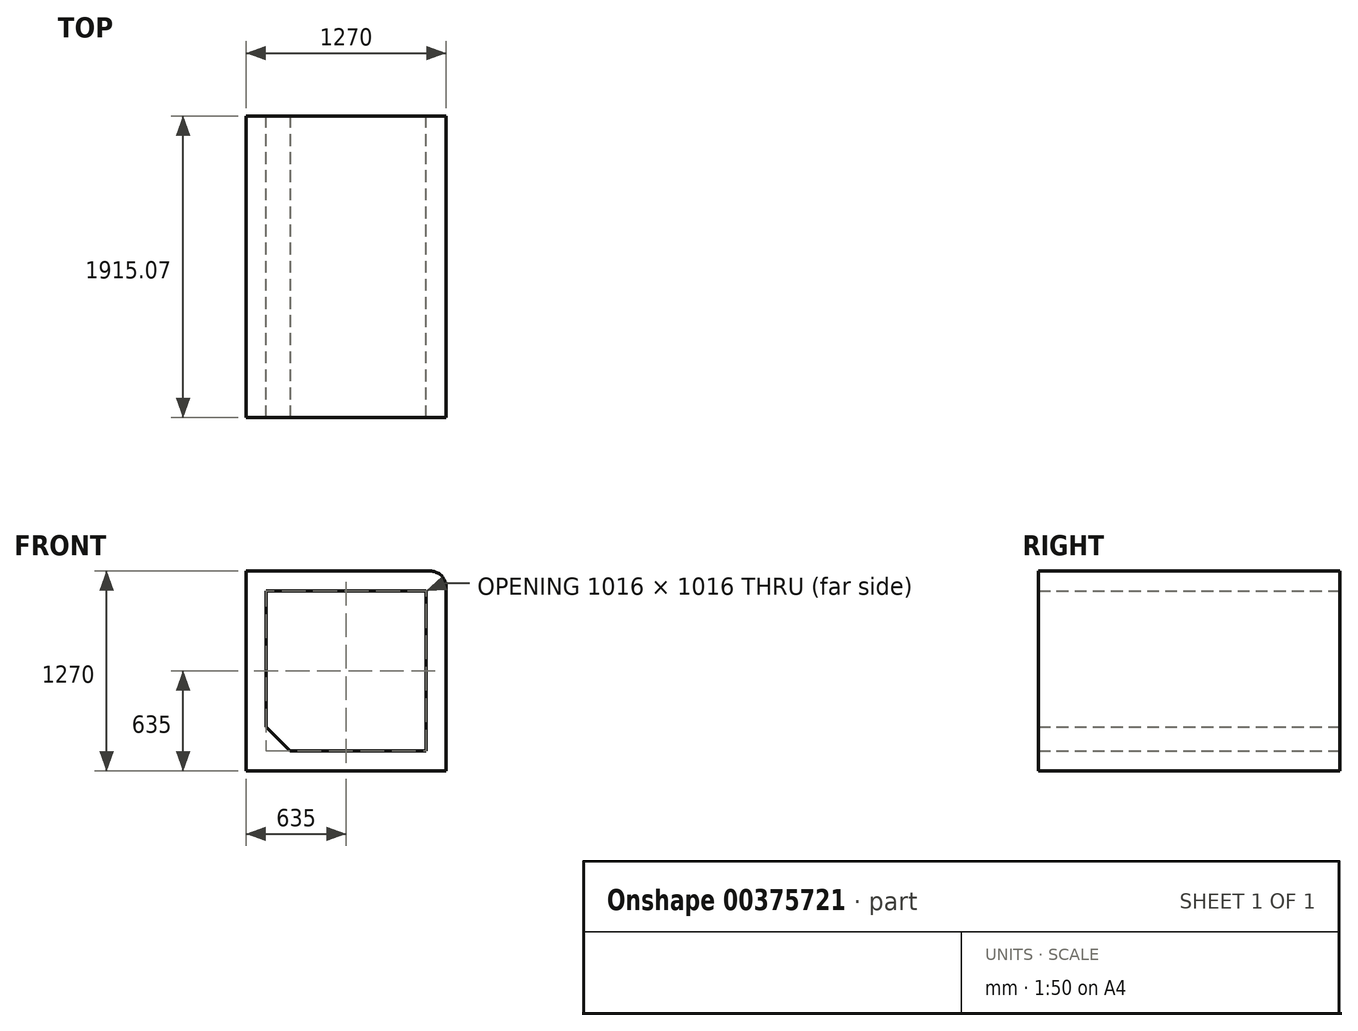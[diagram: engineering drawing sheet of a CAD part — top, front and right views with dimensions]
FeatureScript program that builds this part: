
annotation { "Feature Type Name" : "Feature", "Feature Type Description" : "" }
export const myFeature = defineFeature(function(context is Context, id is Id, definition is map)
    precondition{}
    {
        {
            var Q0;
            Q0=qCreatedBy(makeId("Front.planeOp"),FACE);
            var sketch = newSketch(context, id + "F0", { "sketchPlane" : qUnion([Q0])});
            skLineSegment(sketch, "E0.bottom", {"start": v(508, 508) * mm, "end": v(-508, 508) * mm});
            skLineSegment(sketch, "E0.top", {"start": v(508, -508) * mm, "end": v(-508, -508) * mm});
            skLineSegment(sketch, "E0.left", {"start": v(508, 508) * mm, "end": v(508, -508) * mm});
            skLineSegment(sketch, "E0.right", {"start": v(-508, 508) * mm, "end": v(-508, -508) * mm});
            skPoint(sketch, "E0.middle", {"position": v(0, 0) * mm});
            skLineSegment(sketch, "E1.bottom", {"start": v(635, -635) * mm, "end": v(-635, -635) * mm});
            skLineSegment(sketch, "E1.top", {"start": v(635, 635) * mm, "end": v(-635, 635) * mm});
            skLineSegment(sketch, "E1.left", {"start": v(635, -635) * mm, "end": v(635, 635) * mm});
            skLineSegment(sketch, "E1.right", {"start": v(-635, -635) * mm, "end": v(-635, 635) * mm});
            skSolve(sketch);
        }
        {
            var Q0;
            Q0=makeQuery(id+"F0.imprint","IMPRINT",FACE,{"disambiguationData":[TD([[makeQuery(id+"F0.imprint","IMPRINT",EDGE,{"derivedFrom":sQuery(id+"F0.wireOp",EDGE,"E0.bottom")}),-1.0]])]});
            extrude(context, id + "F1", {"entities" : qUnion([Q0]), "endBound" : BoundingType.SYMMETRIC, "depth" : 1270 * mm});
        }
        {
            var Q0;
            Q0=makeQuery(id+"F1.opExtrude","SWEPT_EDGE",EDGE,{"disambiguationData":[OSD([sQuery(id+"F0.wireOp",EDGE,"E1.top"),sQuery(id+"F0.wireOp",EDGE,"E1.left")])]});
            fillet(context, id + "F2", {"entities" : qUnion([Q0]), "radius" : 101.6 * mm, "tangentPropagation" : true, "allowEdgeOverflow" : false});
        }
        {
            var Q0;
            Q0=makeQuery(id+"F1.opExtrude","SWEPT_EDGE",EDGE,{"disambiguationData":[OSD([sQuery(id+"F0.wireOp",EDGE,"E0.top"),sQuery(id+"F0.wireOp",EDGE,"E0.right")])]});
            chamfer(context, id + "F3", {"entities" : qUnion([Q0]), "width" : 152.4 * mm, "tangentPropagation" : true});
        }
        {
            var Q0;
            Q0=makeQuery(id+"F1.opExtrude","CAP_FACE",FACE,{"disambiguationData":[OSD([sQuery(id+"F0.wireOp",EDGE,"E0.bottom"),sQuery(id+"F0.wireOp",EDGE,"E0.top"),sQuery(id+"F0.wireOp",EDGE,"E0.left"),sQuery(id+"F0.wireOp",EDGE,"E0.right"),sQuery(id+"F0.wireOp",EDGE,"E1.bottom"),sQuery(id+"F0.wireOp",EDGE,"E1.top"),sQuery(id+"F0.wireOp",EDGE,"E1.left"),sQuery(id+"F0.wireOp",EDGE,"E1.right")])],"isStart":false});
            extrude(context, id + "F4", {"entities" : qUnion([Q0]), "operationType" : NewBodyOperationType.ADD, "depth" : 645.07 * mm});
        }
    });
